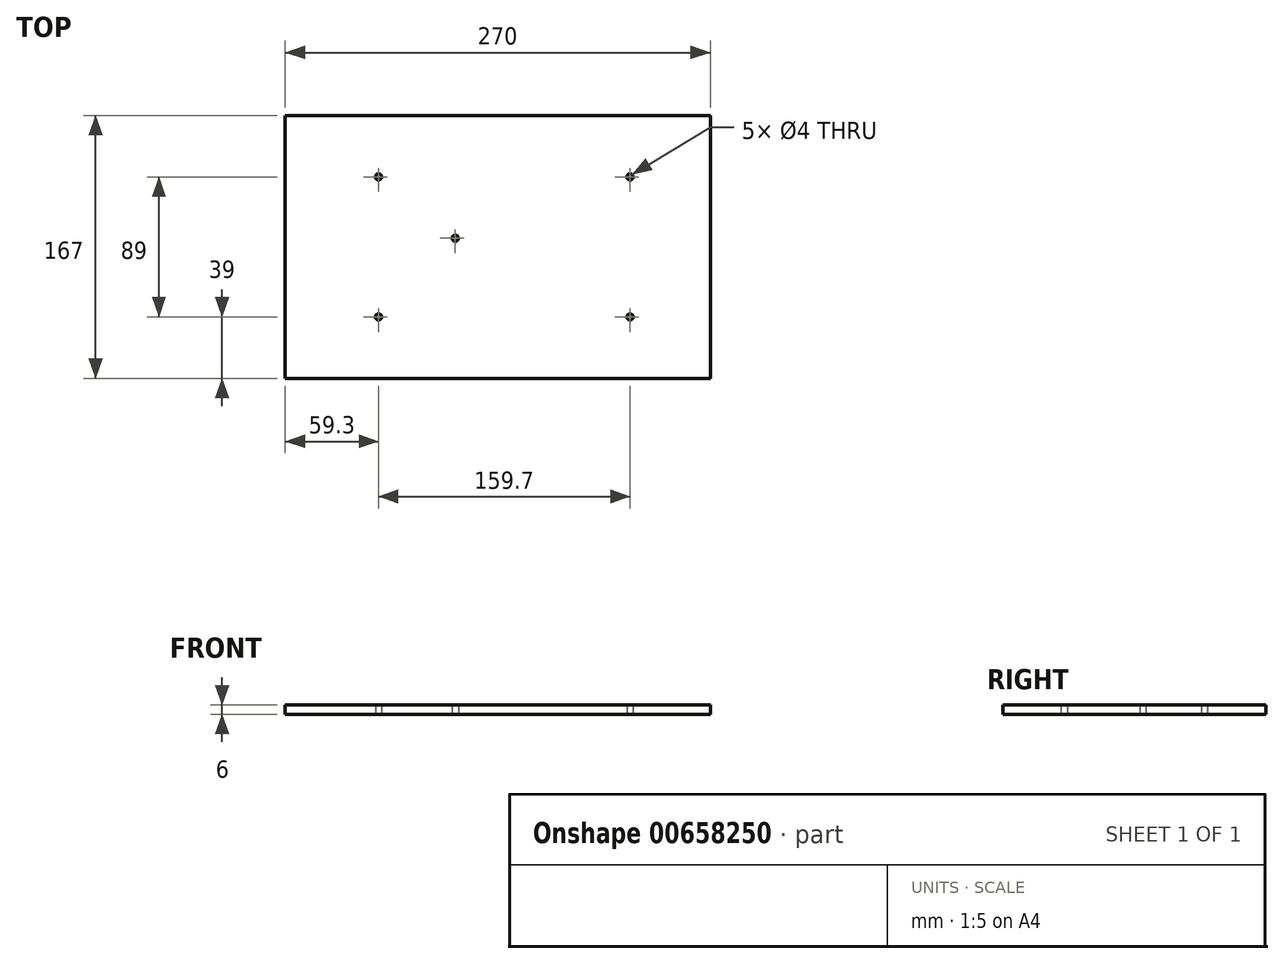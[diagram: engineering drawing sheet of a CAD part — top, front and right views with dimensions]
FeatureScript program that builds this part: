
annotation { "Feature Type Name" : "Feature", "Feature Type Description" : "" }
export const myFeature = defineFeature(function(context is Context, id is Id, definition is map)
    precondition{}
    {
        {
            var Q0;
            Q0=qCreatedBy(makeId("Top.planeOp"),FACE);
            var sketch = newSketch(context, id + "F0", { "sketchPlane" : qUnion([Q0])});
            skLineSegment(sketch, "E0.bottom", {"start": v(-135, 83.5) * mm, "end": v(135, 83.5) * mm});
            skLineSegment(sketch, "E0.top", {"start": v(-135, -83.5) * mm, "end": v(135, -83.5) * mm});
            skLineSegment(sketch, "E0.left", {"start": v(-135, 83.5) * mm, "end": v(-135, -83.5) * mm});
            skLineSegment(sketch, "E0.right", {"start": v(135, 83.5) * mm, "end": v(135, -83.5) * mm});
            skPoint(sketch, "E1", {"position": v(0, 83.5) * mm});
            skPoint(sketch, "E2", {"position": v(-135, 0) * mm});
            skLineSegment(sketch, "E3.bottom", {"start": v(-115, 63.5) * mm, "end": v(115, 63.5) * mm, "construction": true});
            skLineSegment(sketch, "E3.top", {"start": v(-115, -63.5) * mm, "end": v(115, -63.5) * mm, "construction": true});
            skLineSegment(sketch, "E3.left", {"start": v(-115, 63.5) * mm, "end": v(-115, -63.5) * mm, "construction": true});
            skLineSegment(sketch, "E3.right", {"start": v(115, 63.5) * mm, "end": v(115, -63.5) * mm, "construction": true});
            skCircle(sketch, "E4", {"center": v(-75.7, -44.5) * mm, "radius": 2 * mm});
            skCircle(sketch, "E5", {"center": v(-75.7, 44.5) * mm, "radius": 2 * mm});
            skCircle(sketch, "E6", {"center": v(84, 44.5) * mm, "radius": 2 * mm});
            skCircle(sketch, "E7", {"center": v(84, -44.5) * mm, "radius": 2 * mm});
            skCircle(sketch, "E8", {"center": v(-27, 5.5) * mm, "radius": 2 * mm});
            skSolve(sketch);
        }
        {
            var Q0;
            Q0 = qSketchRegion(id + "F0", true);
            extrude(context, id + "F1", {"entities" : qUnion([Q0]), "depth" : 6 * mm, "offsetDistance" : 25 * mm});
        }
    });
